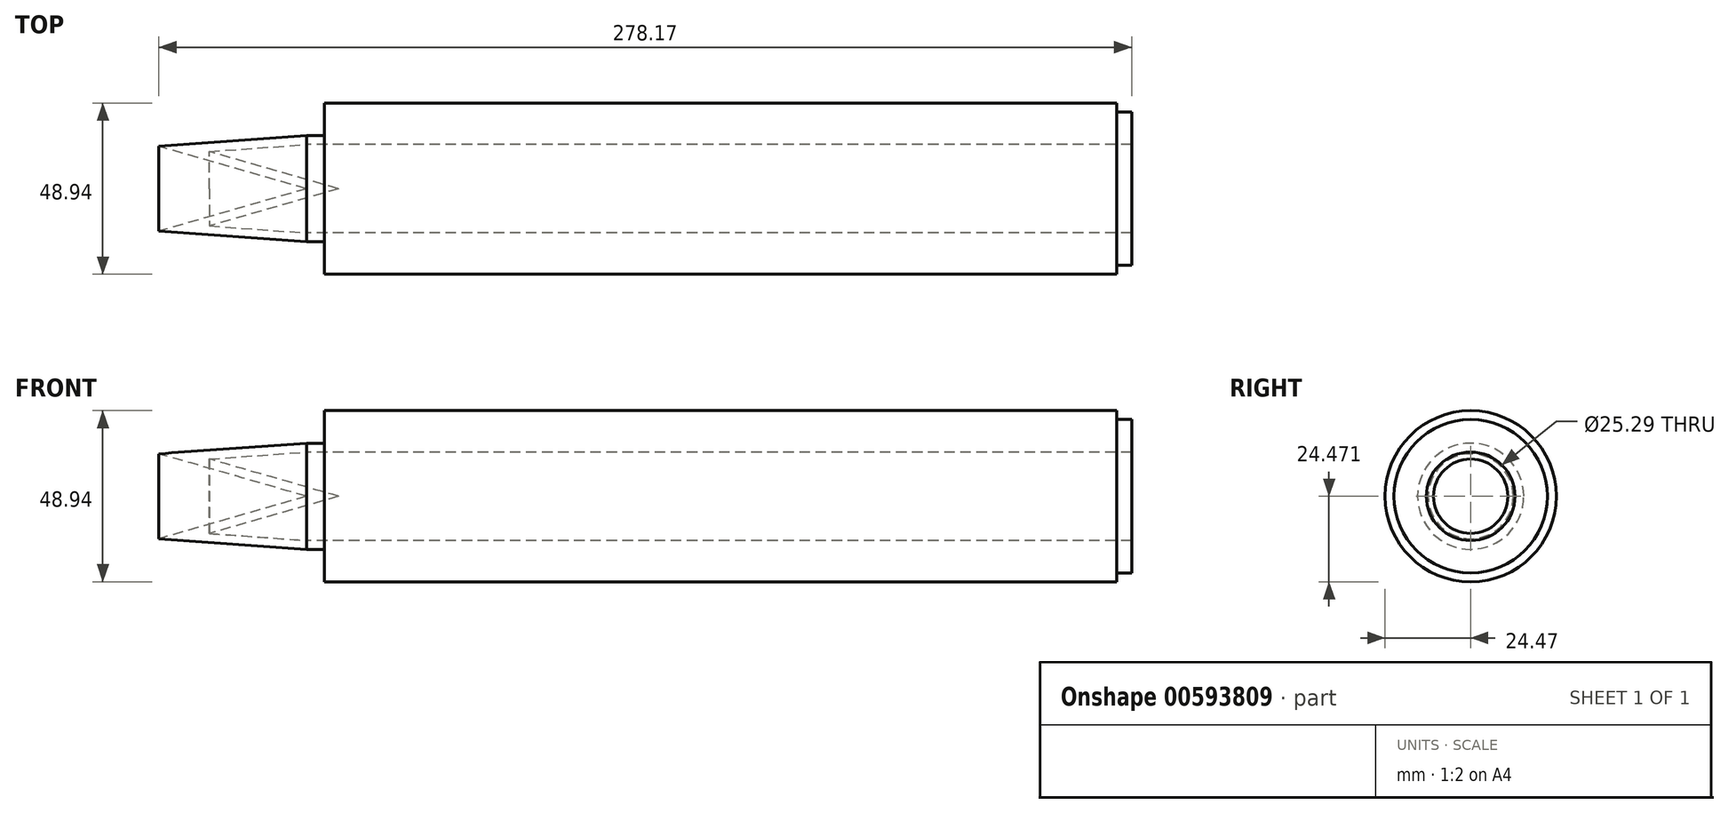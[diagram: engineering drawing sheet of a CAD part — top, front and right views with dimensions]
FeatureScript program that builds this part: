
annotation { "Feature Type Name" : "Feature", "Feature Type Description" : "" }
export const myFeature = defineFeature(function(context is Context, id is Id, definition is map)
    precondition{}
    {
        {
            var Q0;
            Q0=qCreatedBy(makeId("Front.planeOp"),FACE);
            var sketch = newSketch(context, id + "F0", { "sketchPlane" : qUnion([Q0])});
            skLineSegment(sketch, "E0", {"start": v(-87.06, -12.14) * mm, "end": v(144.64, -12.14) * mm});
            skLineSegment(sketch, "E1", {"start": v(144.64, -12.14) * mm, "end": v(144.64, 12.33) * mm});
            skLineSegment(sketch, "E2", {"start": v(144.64, 12.33) * mm, "end": v(-82, 12.33) * mm});
            skLineSegment(sketch, "E3", {"start": v(-82, 12.33) * mm, "end": v(-82, 3.05) * mm});
            skLineSegment(sketch, "E4", {"start": v(-82, 3.05) * mm, "end": v(-87.06, 3.05) * mm});
            skLineSegment(sketch, "E5", {"start": v(-87.06, -12.14) * mm, "end": v(-129.28, 0) * mm});
            skLineSegment(sketch, "E6", {"start": v(-87.06, 3.05) * mm, "end": v(-129.28, 0) * mm});
            skSolve(sketch);
        }
        {
            var Q0;
            Q0=makeQuery(id+"F0.imprint","IMPRINT",FACE,{"disambiguationData":[TD([[makeQuery(id+"F0.imprint","IMPRINT",EDGE,{"derivedFrom":sQuery(id+"F0.wireOp",EDGE,"E0")}),1.0]])]});
            var Q1;
            Q1=sQuery(id+"F0.wireOp",EDGE,"E0");
            revolve(context, id + "F1", {"entities" : qUnion([Q0]), "axis" : qUnion([Q1]), "revolveType" : RevolveType.FULL});
        }
        {
            var Q0;
            Q0=makeQuery(id+"F1.opRevolve","SWEPT_FACE",FACE,{"disambiguationData":[OSD([sQuery(id+"F0.wireOp",EDGE,"E1")])]});
            shell(context, id + "F2", {"entities" : qUnion([Q0]), "thickness" : 2.54 * mm});
        }
        {
            var Q0;
            Q0=makeQuery(id+"F2.opShell","OFFSET_FACE",FACE,{"disambiguationData":[OSD([sQuery(id+"F0.wireOp",EDGE,"nnGtQchB-Z8d7-58Aa-3Zfg-Yb77Hpt7r3CT")])]});
            var Q1;
            Q1=makeQuery(id+"F2.opShell","OFFSET_FACE",FACE,{"disambiguationData":[OSD([sQuery(id+"F0.wireOp",EDGE,"E3")])]});
            extrude(context, id + "F3", {"entities" : qUnion([Q0, Q1]), "operationType" : NewBodyOperationType.ADD, "depth" : 214.38 * mm, "offsetDistance" : 25.4 * mm});
        }
        {
            var Q0;
            Q0=makeQuery(id+"F3.opExtrude","CAP_FACE",FACE,{"disambiguationData":[OSD([sQuery(id+"F0.wireOp",EDGE,"E3")])],"isStart":false});
            extrude(context, id + "F4", {"entities" : qUnion([Q0]), "operationType" : NewBodyOperationType.ADD, "depth" : 13.97 * mm, "offsetDistance" : 25.4 * mm});
        }
    });
